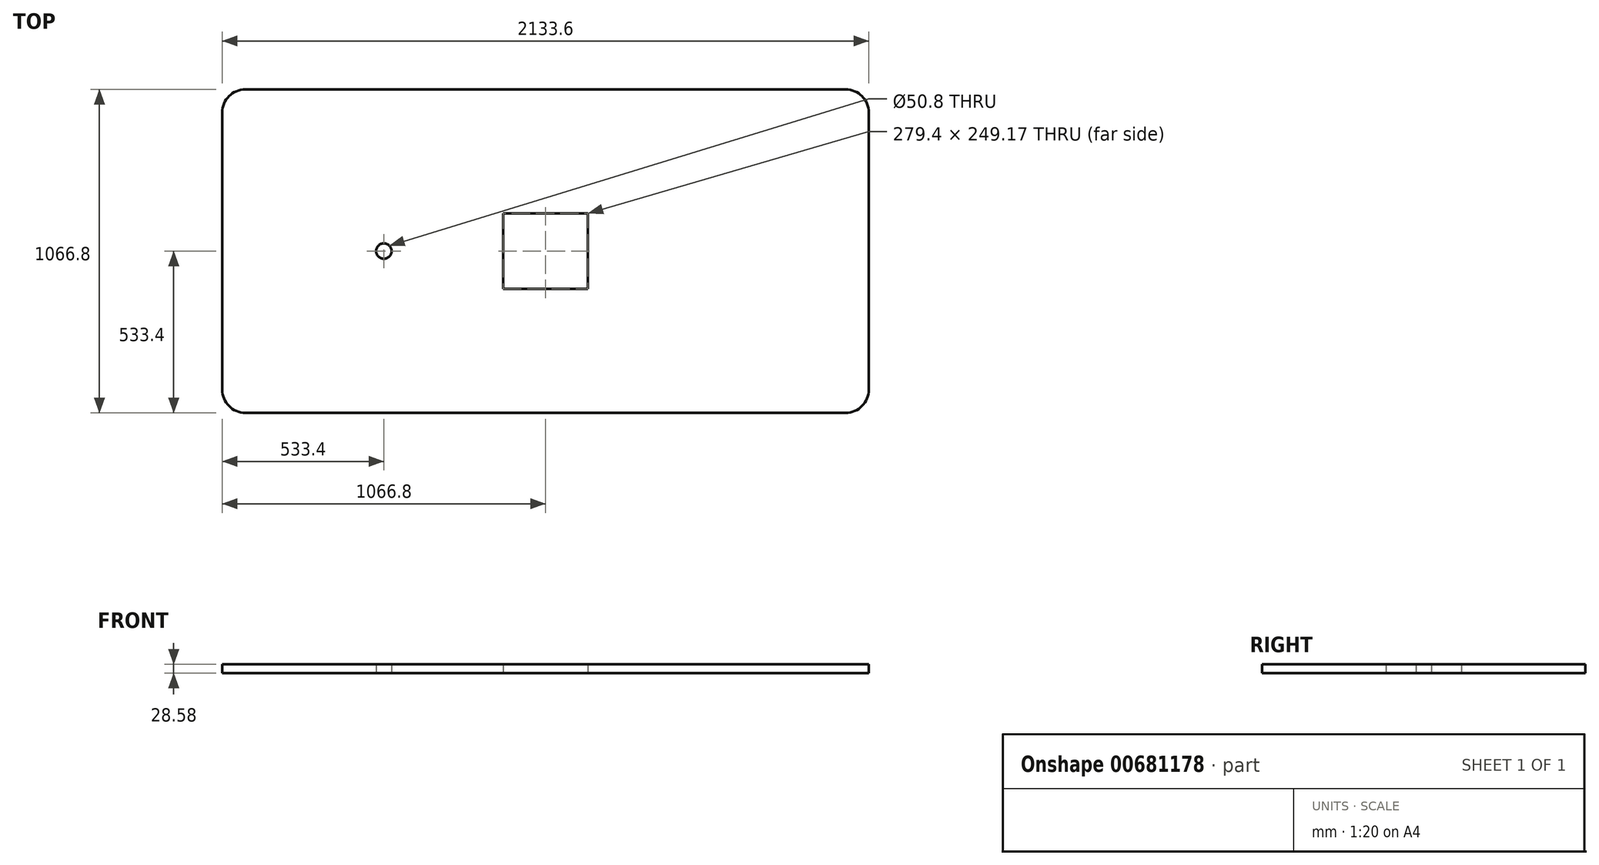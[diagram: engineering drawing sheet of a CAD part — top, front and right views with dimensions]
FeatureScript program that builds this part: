
annotation { "Feature Type Name" : "Feature", "Feature Type Description" : "" }
export const myFeature = defineFeature(function(context is Context, id is Id, definition is map)
    precondition{}
    {
        {
            var Q0;
            Q0=qCreatedBy(makeId("Top.planeOp"),FACE);
            var sketch = newSketch(context, id + "F0", { "sketchPlane" : qUnion([Q0])});
            skLineSegment(sketch, "E0.bottom", {"start": v(-990.6, 533.4) * mm, "end": v(990.6, 533.4) * mm});
            skLineSegment(sketch, "E0.top", {"start": v(-990.6, -533.4) * mm, "end": v(990.6, -533.4) * mm});
            skLineSegment(sketch, "E0.left", {"start": v(-1066.8, 457.2) * mm, "end": v(-1066.8, -457.2) * mm});
            skLineSegment(sketch, "E0.right", {"start": v(1066.8, 457.2) * mm, "end": v(1066.8, -457.2) * mm});
            skPoint(sketch, "E0.middle", {"position": v(0, 0) * mm});
            skLineSegment(sketch, "E1.bottom", {"start": v(139.7, 124.59) * mm, "end": v(-139.7, 124.59) * mm});
            skLineSegment(sketch, "E1.top", {"start": v(139.7, -124.59) * mm, "end": v(-139.7, -124.59) * mm});
            skLineSegment(sketch, "E1.left", {"start": v(139.7, 124.59) * mm, "end": v(139.7, -124.59) * mm});
            skLineSegment(sketch, "E1.right", {"start": v(-139.7, 124.59) * mm, "end": v(-139.7, -124.59) * mm});
            skLineSegment(sketch, "E2", {"start": v(-1066.8, 0) * mm, "end": v(-533.4, 0) * mm});
            skCircle(sketch, "E3", {"center": v(-533.4, 0) * mm, "radius": 25.4 * mm});
            skPoint(sketch, "E4.visualSharp", {"position": v(-1066.8, 533.4) * mm});
            skArc(sketch, "E4.filletArc", {"start": v(-990.6, 533.4) * mm, "mid": v(-1044.48, 511.08) * mm, "end": v(-1066.8, 457.2) * mm});
            skPoint(sketch, "E5.visualSharp", {"position": v(-1066.8, -533.4) * mm});
            skArc(sketch, "E5.filletArc", {"start": v(-1066.8, -457.2) * mm, "mid": v(-1044.48, -511.08) * mm, "end": v(-990.6, -533.4) * mm});
            skPoint(sketch, "E6.visualSharp", {"position": v(1066.8, -533.4) * mm});
            skArc(sketch, "E6.filletArc", {"start": v(990.6, -533.4) * mm, "mid": v(1044.48, -511.08) * mm, "end": v(1066.8, -457.2) * mm});
            skPoint(sketch, "E7.visualSharp", {"position": v(1066.8, 533.4) * mm});
            skArc(sketch, "E7.filletArc", {"start": v(1066.8, 457.2) * mm, "mid": v(1044.48, 511.08) * mm, "end": v(990.6, 533.4) * mm});
            skSolve(sketch);
        }
        {
            var Q0;
            Q0=makeQuery(id+"F0.imprint","IMPRINT",FACE,{"disambiguationData":[TD([[makeQuery(id+"F0.imprint","IMPRINT",EDGE,{"derivedFrom":sQuery(id+"F0.wireOp",EDGE,"E0.bottom")}),-1.0]])]});
            extrude(context, id + "F1", {"entities" : qUnion([Q0]), "depth" : 28.57 * mm, "offsetDistance" : 25.4 * mm});
        }
    });
